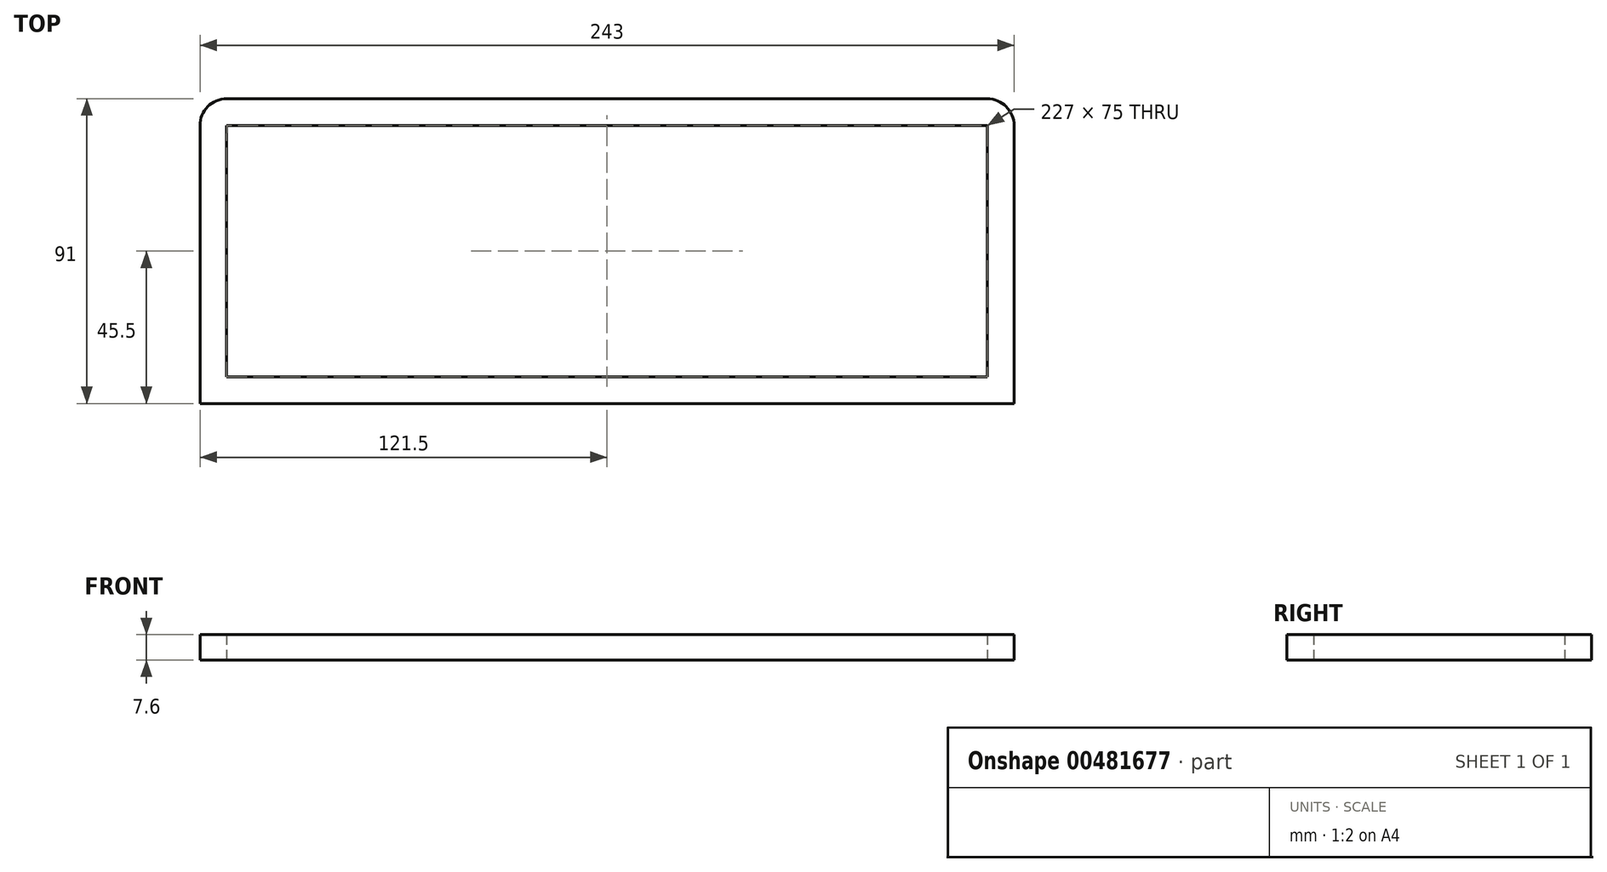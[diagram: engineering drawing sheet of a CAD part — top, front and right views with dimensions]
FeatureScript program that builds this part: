
annotation { "Feature Type Name" : "Feature", "Feature Type Description" : "" }
export const myFeature = defineFeature(function(context is Context, id is Id, definition is map)
    precondition{}
    {
        {
            var Q0;
            Q0=qCreatedBy(makeId("Top.planeOp"),FACE);
            var sketch = newSketch(context, id + "F0", { "sketchPlane" : qUnion([Q0])});
            skLineSegment(sketch, "E0.bottom", {"start": v(0, 0) * mm, "end": v(227, 0) * mm});
            skLineSegment(sketch, "E0.top", {"start": v(0, 75) * mm, "end": v(227, 75) * mm});
            skLineSegment(sketch, "E0.left", {"start": v(0, 0) * mm, "end": v(0, 75) * mm});
            skLineSegment(sketch, "E0.right", {"start": v(227, 0) * mm, "end": v(227, 75) * mm});
            skLineSegment(sketch, "E1.0", {"start": v(0, 83) * mm, "end": v(227, 83) * mm});
            skLineSegment(sketch, "E2.0", {"start": v(235, 0) * mm, "end": v(235, 75) * mm});
            skLineSegment(sketch, "E3.0", {"start": v(-8, 0) * mm, "end": v(-8, 75) * mm});
            skLineSegment(sketch, "E4.0", {"start": v(0, -8) * mm, "end": v(227, -8) * mm});
            skArc(sketch, "E5", {"start": v(-8, 75) * mm, "mid": v(-5.66, 80.66) * mm, "end": v(0, 83) * mm});
            skLineSegment(sketch, "E6", {"start": v(-8, 0) * mm, "end": v(-8, -8) * mm});
            skLineSegment(sketch, "E7", {"start": v(-8, -8) * mm, "end": v(0, -8) * mm});
            skLineSegment(sketch, "E8", {"start": v(235, 0) * mm, "end": v(235, -8) * mm});
            skLineSegment(sketch, "E9", {"start": v(235, -8) * mm, "end": v(227, -8) * mm});
            skArc(sketch, "E10", {"start": v(227, 83) * mm, "mid": v(232.66, 80.66) * mm, "end": v(235, 75) * mm});
            skSolve(sketch);
        }
        {
            var Q0;
            Q0 = qSketchRegion(id + "F0", true);
            extrude(context, id + "F1", {"entities" : qUnion([Q0]), "depth" : 7.6 * mm});
        }
    });
